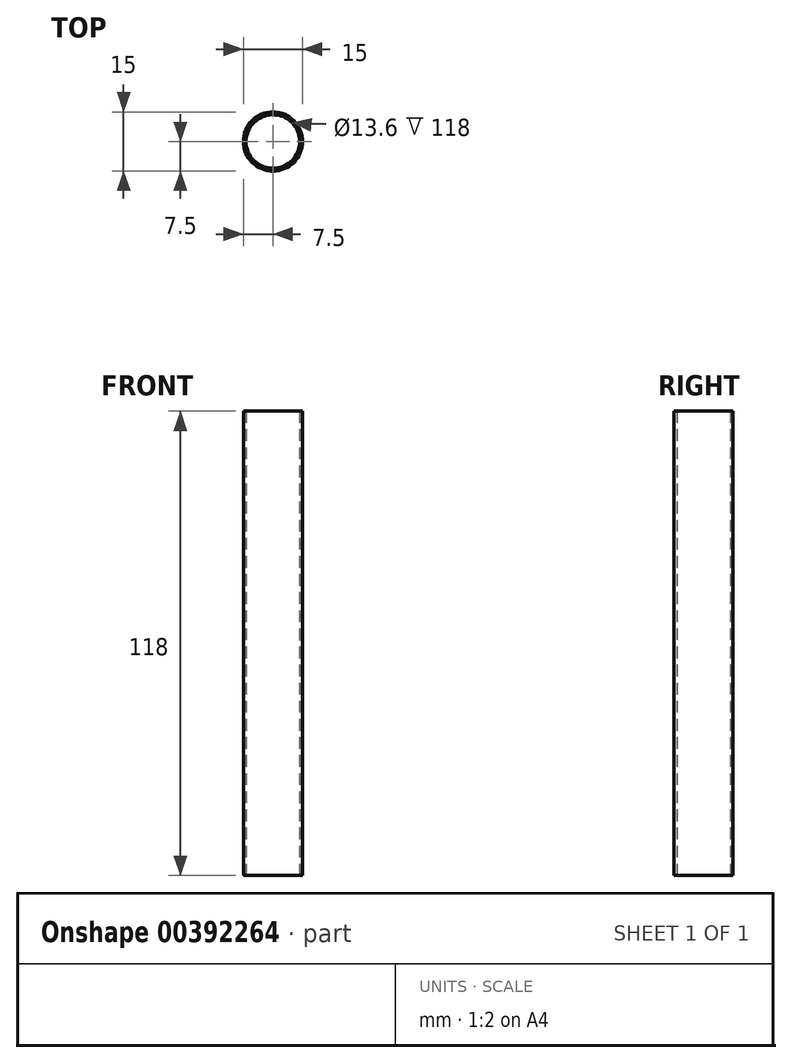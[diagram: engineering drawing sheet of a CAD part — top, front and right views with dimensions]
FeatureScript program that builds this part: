
annotation { "Feature Type Name" : "Feature", "Feature Type Description" : "" }
export const myFeature = defineFeature(function(context is Context, id is Id, definition is map)
    precondition{}
    {
        {
            var Q0;
            Q0=qCreatedBy(makeId("Top.planeOp"),FACE);
            var sketch = newSketch(context, id + "F0", { "sketchPlane" : qUnion([Q0])});
            skCircle(sketch, "E0", {"center": v(0, 0) * mm, "radius": 7.5 * mm});
            skCircle(sketch, "E1", {"center": v(0, 0) * mm, "radius": 6.8 * mm});
            skSolve(sketch);
        }
        {
            var Q0;
            Q0=makeQuery(id+"F0.imprint","IMPRINT",FACE,{"disambiguationData":[TD([[makeQuery(id+"F0.imprint","IMPRINT",EDGE,{"derivedFrom":sQuery(id+"F0.wireOp",EDGE,"E0")}),1.0]])]});
            extrude(context, id + "F1", {"entities" : qUnion([Q0]), "depth" : 118 * mm});
        }
    });
